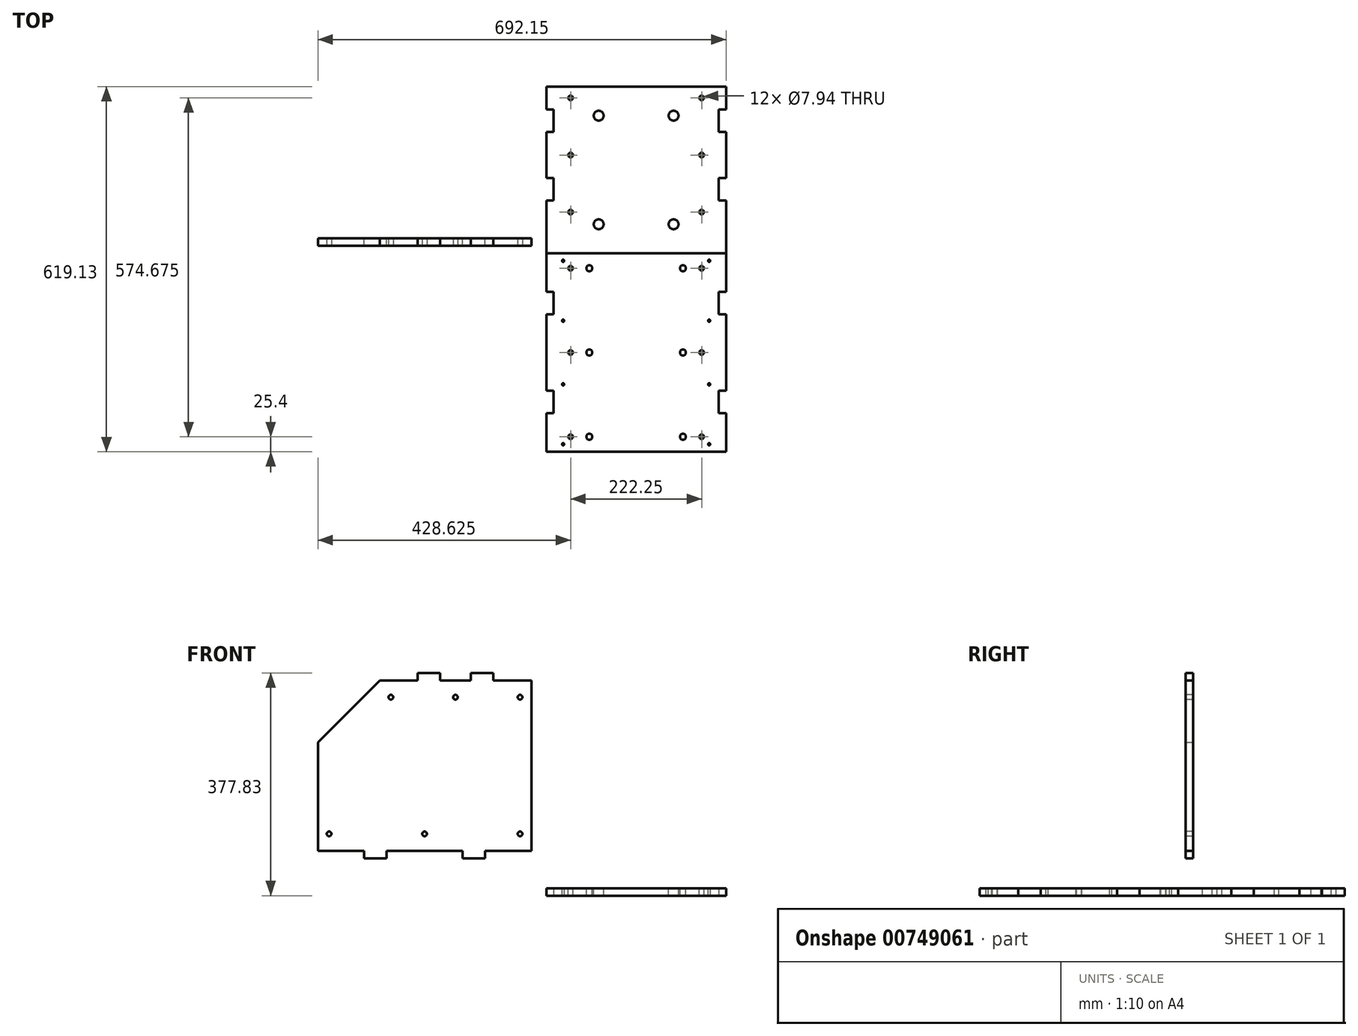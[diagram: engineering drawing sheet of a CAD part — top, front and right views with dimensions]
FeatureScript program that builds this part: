
annotation { "Feature Type Name" : "Feature", "Feature Type Description" : "" }
export const myFeature = defineFeature(function(context is Context, id is Id, definition is map)
    precondition{}
    {
        {
            var Q0;
            Q0=qCreatedBy(makeId("Front.planeOp"),FACE);
            var sketch = newSketch(context, id + "F0", { "sketchPlane" : qUnion([Q0])});
            skLineSegment(sketch, "E0", {"start": v(0, 76.2) * mm, "end": v(-78.1, 76.2) * mm});
            skLineSegment(sketch, "E1", {"start": v(-361.95, 76.2) * mm, "end": v(-361.95, 260.35) * mm});
            skLineSegment(sketch, "E2", {"start": v(-361.95, 260.35) * mm, "end": v(-257.18, 365.12) * mm});
            skLineSegment(sketch, "E3", {"start": v(-257.18, 365.12) * mm, "end": v(-192.85, 365.12) * mm});
            skLineSegment(sketch, "E4", {"start": v(0, 365.13) * mm, "end": v(0, 76.2) * mm});
            skLineSegment(sketch, "E5", {"start": v(-128.59, 365.13) * mm, "end": v(-128.59, 193.45) * mm, "construction": true});
            skLineSegment(sketch, "E6", {"start": v(-180.98, 76.2) * mm, "end": v(-180.98, 177) * mm, "construction": true});
            skLineSegment(sketch, "E7.top", {"start": v(-154.75, 377.83) * mm, "end": v(-192.85, 377.83) * mm});
            skLineSegment(sketch, "E7.left", {"start": v(-154.75, 365.13) * mm, "end": v(-154.75, 377.83) * mm});
            skLineSegment(sketch, "E7.right", {"start": v(-192.85, 365.12) * mm, "end": v(-192.85, 377.83) * mm});
            skPoint(sketch, "E7.middle", {"position": v(-199.2, 365.12) * mm});
            skLineSegment(sketch, "E8.MirrorCS", {"start": v(-102.43, 365.13) * mm, "end": v(-102.43, 377.82) * mm});
            skLineSegment(sketch, "E9.MirrorCS", {"start": v(-102.43, 377.83) * mm, "end": v(-64.33, 377.83) * mm});
            skLineSegment(sketch, "E10.MirrorCS", {"start": v(-64.33, 365.13) * mm, "end": v(-64.33, 377.83) * mm});
            skLineSegment(sketch, "E11.trimOffspring", {"start": v(-64.33, 365.13) * mm, "end": v(0, 365.13) * mm});
            skLineSegment(sketch, "E12.trimOffspring", {"start": v(-154.75, 365.13) * mm, "end": v(-102.43, 365.13) * mm});
            skLineSegment(sketch, "E13.bottom", {"start": v(-245.75, 63.5) * mm, "end": v(-283.85, 63.5) * mm});
            skLineSegment(sketch, "E13.left", {"start": v(-245.75, 63.5) * mm, "end": v(-245.75, 76.2) * mm});
            skLineSegment(sketch, "E13.right", {"start": v(-283.85, 63.5) * mm, "end": v(-283.85, 76.2) * mm});
            skPoint(sketch, "E13.middle", {"position": v(-264.8, 76.2) * mm});
            skLineSegment(sketch, "E14.trimOffspring", {"start": v(-283.85, 76.2) * mm, "end": v(-361.95, 76.2) * mm});
            skLineSegment(sketch, "E15.MirrorCS", {"start": v(-116.2, 63.5) * mm, "end": v(-116.2, 76.2) * mm});
            skLineSegment(sketch, "E16.MirrorCS", {"start": v(-116.2, 63.5) * mm, "end": v(-78.1, 63.5) * mm});
            skLineSegment(sketch, "E17.MirrorCS", {"start": v(-78.1, 63.5) * mm, "end": v(-78.1, 76.2) * mm});
            skLineSegment(sketch, "E18.trimOffspring", {"start": v(-116.2, 76.2) * mm, "end": v(-245.75, 76.2) * mm});
            skLineSegment(sketch, "E19", {"start": v(-361.95, 104.77) * mm, "end": v(0, 104.78) * mm, "construction": true});
            skLineSegment(sketch, "E20", {"start": v(0, 336.55) * mm, "end": v(-285.75, 336.55) * mm, "construction": true});
            skPoint(sketch, "E21", {"position": v(-128.59, 336.55) * mm});
            skPoint(sketch, "E22", {"position": v(-19.05, 336.55) * mm});
            skPoint(sketch, "E23", {"position": v(-19.05, 104.78) * mm});
            skPoint(sketch, "E24", {"position": v(-180.98, 104.77) * mm});
            skPoint(sketch, "E25.MirrorP", {"position": v(-238.13, 336.55) * mm});
            skPoint(sketch, "E26.MirrorP", {"position": v(-342.9, 104.78) * mm});
            skSolve(sketch);
        }
        {
            var Q0;
            Q0 = qSketchRegion(id + "F0", true);
            extrude(context, id + "F1", {"entities" : qUnion([Q0]), "depth" : 12.7 * mm, "offsetDistance" : 25.4 * mm});
        }
        {
            var Q0;
            Q0=qCreatedBy(makeId("Top.planeOp"),FACE);
            var sketch = newSketch(context, id + "F2", { "sketchPlane" : qUnion([Q0])});
            skLineSegment(sketch, "E27.bottom", {"start": v(25.4, 25.4) * mm, "end": v(330.2, 25.4) * mm});
            skLineSegment(sketch, "E27.top", {"start": v(25.4, 257.18) * mm, "end": v(330.2, 257.18) * mm});
            skLineSegment(sketch, "E27.left", {"start": v(25.4, 25.4) * mm, "end": v(25.4, 64.33) * mm});
            skLineSegment(sketch, "E27.right", {"start": v(330.2, 25.4) * mm, "end": v(330.2, 64.33) * mm});
            skLineSegment(sketch, "E28", {"start": v(177.8, 25.4) * mm, "end": v(177.8, 257.17) * mm, "construction": true});
            skLineSegment(sketch, "E29", {"start": v(25.4, 141.29) * mm, "end": v(330.2, 141.29) * mm, "construction": true});
            skLineSegment(sketch, "E30.bottom", {"start": v(38.1, 180.15) * mm, "end": v(25.4, 180.15) * mm});
            skLineSegment(sketch, "E30.top", {"start": v(38.1, 218.25) * mm, "end": v(25.4, 218.25) * mm});
            skLineSegment(sketch, "E30.left", {"start": v(38.1, 180.15) * mm, "end": v(38.1, 218.25) * mm});
            skPoint(sketch, "E30.middle", {"position": v(25.4, 199.2) * mm});
            skPoint(sketch, "E31.orphan", {"position": v(12.7, 218.25) * mm});
            skLineSegment(sketch, "E32.trimOffspring", {"start": v(25.4, 218.25) * mm, "end": v(25.4, 257.18) * mm});
            skPoint(sketch, "E33.orphan", {"position": v(12.7, 180.15) * mm});
            skLineSegment(sketch, "E34.MirrorCS", {"start": v(317.5, 180.15) * mm, "end": v(317.5, 218.25) * mm});
            skLineSegment(sketch, "E35.MirrorCS", {"start": v(317.5, 218.25) * mm, "end": v(330.2, 218.25) * mm});
            skLineSegment(sketch, "E36.MirrorCS", {"start": v(317.5, 180.15) * mm, "end": v(330.2, 180.15) * mm});
            skLineSegment(sketch, "E37.MirrorCS", {"start": v(38.1, 102.43) * mm, "end": v(25.4, 102.43) * mm});
            skLineSegment(sketch, "E38.MirrorCS", {"start": v(38.1, 102.43) * mm, "end": v(38.1, 64.33) * mm});
            skLineSegment(sketch, "E39.MirrorCS", {"start": v(38.1, 64.33) * mm, "end": v(25.4, 64.33) * mm});
            skLineSegment(sketch, "E40.MirrorCS", {"start": v(317.5, 102.43) * mm, "end": v(317.5, 64.33) * mm});
            skLineSegment(sketch, "E41.MirrorCS", {"start": v(317.5, 64.33) * mm, "end": v(330.2, 64.33) * mm});
            skLineSegment(sketch, "E42.MirrorCS", {"start": v(317.5, 102.43) * mm, "end": v(330.2, 102.43) * mm});
            skLineSegment(sketch, "E43.trimOffspring", {"start": v(25.4, 102.43) * mm, "end": v(25.4, 199.2) * mm});
            skLineSegment(sketch, "E44.trimOffspring", {"start": v(330.2, 102.43) * mm, "end": v(330.2, 180.15) * mm});
            skLineSegment(sketch, "E45.trimOffspring", {"start": v(330.2, 218.25) * mm, "end": v(330.2, 257.18) * mm});
            skPoint(sketch, "E46", {"position": v(241.3, 207.96) * mm});
            skPoint(sketch, "E47", {"position": v(241.3, 23.81) * mm});
            skPoint(sketch, "E48.MirrorP", {"position": v(114.3, 207.96) * mm});
            skPoint(sketch, "E49.MirrorP", {"position": v(114.3, 23.81) * mm});
            skPoint(sketch, "E50", {"position": v(66.67, 238.13) * mm});
            skPoint(sketch, "E51", {"position": v(66.67, 141.29) * mm});
            skPoint(sketch, "E52.MirrorP", {"position": v(66.68, 44.45) * mm});
            skPoint(sketch, "E53.MirrorP", {"position": v(288.92, 238.13) * mm});
            skPoint(sketch, "E54.MirrorP", {"position": v(288.93, 141.29) * mm});
            skPoint(sketch, "E55.MirrorP", {"position": v(288.93, 44.45) * mm});
            skLineSegment(sketch, "E56.top", {"start": v(25.4, -25.4) * mm, "end": v(330.2, -25.4) * mm});
            skLineSegment(sketch, "E56.left", {"start": v(25.4, 25.4) * mm, "end": v(25.4, -25.4) * mm});
            skLineSegment(sketch, "E56.right", {"start": v(330.2, 25.4) * mm, "end": v(330.2, -25.4) * mm});
            skSolve(sketch);
        }
        {
            var Q0;
            Q0 = qSketchRegion(id + "F2", true);
            extrude(context, id + "F3", {"entities" : qUnion([Q0]), "depth" : 12.7 * mm, "offsetDistance" : 25.4 * mm});
        }
        {
            var Q0;
            Q0=sQuery(id+"F2.wireOp",VERTEX,"E50");
            var Q1;
            Q1=sQuery(id+"F2.wireOp",VERTEX,"E51");
            var Q2;
            Q2=sQuery(id+"F2.wireOp",VERTEX,"E52.MirrorP");
            var Q3;
            Q3=sQuery(id+"F2.wireOp",VERTEX,"E53.MirrorP");
            var Q4;
            Q4=sQuery(id+"F2.wireOp",VERTEX,"E54.MirrorP");
            var Q5;
            Q5=sQuery(id+"F2.wireOp",VERTEX,"E55.MirrorP");
            var Q6;
            Q6=makeQuery(id+"F3.opExtrude","SWEPT_BODY",BODY,{"disambiguationData":[OSD([sQuery(id+"F2.wireOp",EDGE,"E27.bottom"),sQuery(id+"F2.wireOp",EDGE,"E27.top"),sQuery(id+"F2.wireOp",EDGE,"E27.left"),sQuery(id+"F2.wireOp",EDGE,"E27.right"),sQuery(id+"F2.wireOp",EDGE,"E30.bottom"),sQuery(id+"F2.wireOp",EDGE,"E30.top"),sQuery(id+"F2.wireOp",EDGE,"E30.left"),sQuery(id+"F2.wireOp",EDGE,"E32.trimOffspring"),sQuery(id+"F2.wireOp",EDGE,"E34.MirrorCS"),sQuery(id+"F2.wireOp",EDGE,"E35.MirrorCS"),sQuery(id+"F2.wireOp",EDGE,"E36.MirrorCS"),sQuery(id+"F2.wireOp",EDGE,"E37.MirrorCS"),sQuery(id+"F2.wireOp",EDGE,"E38.MirrorCS"),sQuery(id+"F2.wireOp",EDGE,"E39.MirrorCS"),sQuery(id+"F2.wireOp",EDGE,"E41.MirrorCS"),sQuery(id+"F2.wireOp",EDGE,"E40.MirrorCS"),sQuery(id+"F2.wireOp",EDGE,"E42.MirrorCS"),sQuery(id+"F2.wireOp",EDGE,"E43.trimOffspring"),sQuery(id+"F2.wireOp",EDGE,"E44.trimOffspring"),sQuery(id+"F2.wireOp",EDGE,"E45.trimOffspring")])]});
            hole(context, id + "F4", {"style" : HoleStyle.SIMPLE, "endStyle" : HoleEndStyle.BLIND, "oppositeDirection" : true, "standardTappedOrClearance" : lookupTablePath({ "standard" : "ANSI", "engagement" : "75%", "pitch" : "16 tpi", "size" : "3/8", "type" : "Tapped" }), "standardBlindInLast" : lookupTablePath({ "standard" : "ANSI", "engagement" : "75%", "pitch" : "16 tpi", "size" : "3/8", "type" : "Tapped" }), "holeDiameter" : 7.94 * mm, "majorDiameter" : 9.52 * mm, "showTappedDepth" : true, "holeDepth" : 20.65 * mm, "isTappedThrough" : true, "tappedDepth" : 15.9 * mm, "tapClearance" : 3, "locations" : qUnion([Q0, Q1, Q2, Q3, Q4, Q5]), "scope" : qUnion([Q6])});
        }
        {
            var Q0;
            Q0=sQuery(id+"F2.wireOp",VERTEX,"E48.MirrorP");
            var Q1;
            Q1=sQuery(id+"F2.wireOp",VERTEX,"E49.MirrorP");
            var Q2;
            Q2=sQuery(id+"F2.wireOp",VERTEX,"E47");
            var Q3;
            Q3=sQuery(id+"F2.wireOp",VERTEX,"E46");
            var Q4;
            Q4=makeQuery(id+"F3.opExtrude","SWEPT_BODY",BODY,{"disambiguationData":[OSD([sQuery(id+"F2.wireOp",EDGE,"E27.bottom"),sQuery(id+"F2.wireOp",EDGE,"E27.top"),sQuery(id+"F2.wireOp",EDGE,"E27.left"),sQuery(id+"F2.wireOp",EDGE,"E27.right"),sQuery(id+"F2.wireOp",EDGE,"E30.bottom"),sQuery(id+"F2.wireOp",EDGE,"E30.top"),sQuery(id+"F2.wireOp",EDGE,"E30.left"),sQuery(id+"F2.wireOp",EDGE,"E32.trimOffspring"),sQuery(id+"F2.wireOp",EDGE,"E34.MirrorCS"),sQuery(id+"F2.wireOp",EDGE,"E35.MirrorCS"),sQuery(id+"F2.wireOp",EDGE,"E36.MirrorCS"),sQuery(id+"F2.wireOp",EDGE,"E37.MirrorCS"),sQuery(id+"F2.wireOp",EDGE,"E38.MirrorCS"),sQuery(id+"F2.wireOp",EDGE,"E39.MirrorCS"),sQuery(id+"F2.wireOp",EDGE,"E41.MirrorCS"),sQuery(id+"F2.wireOp",EDGE,"E40.MirrorCS"),sQuery(id+"F2.wireOp",EDGE,"E42.MirrorCS"),sQuery(id+"F2.wireOp",EDGE,"E43.trimOffspring"),sQuery(id+"F2.wireOp",EDGE,"E44.trimOffspring"),sQuery(id+"F2.wireOp",EDGE,"E45.trimOffspring")])]});
            hole(context, id + "F5", {"style" : HoleStyle.SIMPLE, "endStyle" : HoleEndStyle.BLIND, "oppositeDirection" : true, "standardTappedOrClearance" : lookupTablePath({ "fit" : "Normal (ASME)", "standard" : "ANSI", "size" : "5/8", "type" : "Clearance" }), "standardBlindInLast" : lookupTablePath({ "fit" : "Free", "standard" : "ANSI", "size" : "5/8", "type" : "Clearance" }), "holeDiameter" : 16.67 * mm, "majorDiameter" : 15.88 * mm, "holeDepth" : 22.8 * mm, "isTappedThrough" : true, "tappedDepth" : 15.9 * mm, "tapClearance" : 3, "locations" : qUnion([Q0, Q1, Q2, Q3]), "scope" : qUnion([Q4])});
        }
        {
            var Q0;
            Q0=qCreatedBy(makeId("Top.planeOp"),FACE);
            var sketch = newSketch(context, id + "F6", { "sketchPlane" : qUnion([Q0])});
            skLineSegment(sketch, "E57.bottom", {"start": v(25.4, -25.4) * mm, "end": v(330.2, -25.4) * mm});
            skLineSegment(sketch, "E57.top", {"start": v(25.4, -361.95) * mm, "end": v(330.2, -361.95) * mm});
            skLineSegment(sketch, "E57.left", {"start": v(25.4, -25.4) * mm, "end": v(25.4, -90.8) * mm});
            skLineSegment(sketch, "E57.right", {"start": v(330.2, -25.4) * mm, "end": v(330.2, -90.8) * mm});
            skLineSegment(sketch, "E58", {"start": v(177.8, -361.95) * mm, "end": v(177.8, -25.4) * mm, "construction": true});
            skLineSegment(sketch, "E59", {"start": v(330.2, -193.67) * mm, "end": v(25.4, -193.67) * mm, "construction": true});
            skLineSegment(sketch, "E60.bottom", {"start": v(317.5, -258.44) * mm, "end": v(330.2, -258.44) * mm});
            skLineSegment(sketch, "E60.top", {"start": v(317.5, -296.54) * mm, "end": v(330.2, -296.54) * mm});
            skLineSegment(sketch, "E60.left", {"start": v(317.5, -258.44) * mm, "end": v(317.5, -296.54) * mm});
            skPoint(sketch, "E60.middle", {"position": v(330.2, -277.5) * mm});
            skPoint(sketch, "E61.orphan", {"position": v(342.9, -296.54) * mm});
            skPoint(sketch, "E62.orphan", {"position": v(342.9, -258.44) * mm});
            skLineSegment(sketch, "E63.trimOffspring", {"start": v(330.2, -296.54) * mm, "end": v(330.2, -361.95) * mm});
            skLineSegment(sketch, "E64.MirrorCS", {"start": v(38.1, -296.54) * mm, "end": v(25.4, -296.54) * mm});
            skLineSegment(sketch, "E65.MirrorCS", {"start": v(38.1, -258.44) * mm, "end": v(38.1, -296.54) * mm});
            skLineSegment(sketch, "E66.MirrorCS", {"start": v(38.1, -258.44) * mm, "end": v(25.4, -258.44) * mm});
            skLineSegment(sketch, "E67.trimOffspring", {"start": v(25.4, -296.54) * mm, "end": v(25.4, -361.95) * mm});
            skLineSegment(sketch, "E68.MirrorCS", {"start": v(317.5, -128.9) * mm, "end": v(330.2, -128.9) * mm});
            skLineSegment(sketch, "E69.MirrorCS", {"start": v(317.5, -128.9) * mm, "end": v(317.5, -90.8) * mm});
            skLineSegment(sketch, "E70.MirrorCS", {"start": v(317.5, -90.8) * mm, "end": v(330.2, -90.8) * mm});
            skLineSegment(sketch, "E71.MirrorCS", {"start": v(38.1, -128.9) * mm, "end": v(38.1, -90.8) * mm});
            skLineSegment(sketch, "E72.MirrorCS", {"start": v(38.1, -90.8) * mm, "end": v(25.4, -90.8) * mm});
            skLineSegment(sketch, "E73.MirrorCS", {"start": v(38.1, -128.9) * mm, "end": v(25.4, -128.9) * mm});
            skLineSegment(sketch, "E74.trimOffspring", {"start": v(330.2, -128.9) * mm, "end": v(330.2, -258.44) * mm});
            skLineSegment(sketch, "E75.trimOffspring", {"start": v(25.4, -128.9) * mm, "end": v(25.4, -258.44) * mm});
            skPoint(sketch, "E76", {"position": v(66.68, -336.55) * mm});
            skPoint(sketch, "E77", {"position": v(66.68, -193.67) * mm});
            skPoint(sketch, "E78.MirrorP", {"position": v(66.67, -50.8) * mm});
            skPoint(sketch, "E79.MirrorP", {"position": v(288.93, -336.55) * mm});
            skPoint(sketch, "E80.MirrorP", {"position": v(288.93, -193.67) * mm});
            skPoint(sketch, "E81.MirrorP", {"position": v(288.93, -50.8) * mm});
            skPoint(sketch, "E82", {"position": v(98.43, -336.55) * mm});
            skPoint(sketch, "E83", {"position": v(98.42, -193.67) * mm});
            skPoint(sketch, "E84.MirrorP", {"position": v(98.42, -50.8) * mm});
            skPoint(sketch, "E85", {"position": v(53.98, -349.25) * mm});
            skPoint(sketch, "E86.MirrorP", {"position": v(53.97, -38.1) * mm});
            skPoint(sketch, "E87", {"position": v(53.98, -247.65) * mm});
            skPoint(sketch, "E88.MirrorP", {"position": v(53.97, -139.7) * mm});
            skLineSegment(sketch, "E89.MirrorCS", {"start": v(177.8, -25.4) * mm, "end": v(177.8, -361.95) * mm, "construction": true});
            skPoint(sketch, "E90.MirrorP", {"position": v(257.18, -193.67) * mm});
            skPoint(sketch, "E91.MirrorP", {"position": v(301.62, -139.7) * mm});
            skPoint(sketch, "E92.MirrorP", {"position": v(288.92, -50.8) * mm});
            skPoint(sketch, "E93.MirrorP", {"position": v(301.62, -38.1) * mm});
            skPoint(sketch, "E94.MirrorP", {"position": v(301.63, -247.65) * mm});
            skPoint(sketch, "E95.MirrorP", {"position": v(301.63, -349.25) * mm});
            skPoint(sketch, "E96.MirrorP", {"position": v(257.18, -336.55) * mm});
            skPoint(sketch, "E97.MirrorP", {"position": v(257.17, -50.8) * mm});
            skSolve(sketch);
        }
        {
            var Q0;
            Q0=sQuery(id+"F0.wireOp",VERTEX,"E25.MirrorP");
            var Q1;
            Q1=sQuery(id+"F0.wireOp",VERTEX,"E22");
            var Q2;
            Q2=sQuery(id+"F0.wireOp",VERTEX,"E21");
            var Q3;
            Q3=sQuery(id+"F0.wireOp",VERTEX,"E26.MirrorP");
            var Q4;
            Q4=sQuery(id+"F0.wireOp",VERTEX,"E24");
            var Q5;
            Q5=sQuery(id+"F0.wireOp",VERTEX,"E23");
            var Q6;
            Q6=makeQuery(id+"F1.opExtrude","SWEPT_BODY",BODY,{"disambiguationData":[OSD([sQuery(id+"F0.wireOp",EDGE,"E0"),sQuery(id+"F0.wireOp",EDGE,"E1"),sQuery(id+"F0.wireOp",EDGE,"E2"),sQuery(id+"F0.wireOp",EDGE,"E3"),sQuery(id+"F0.wireOp",EDGE,"E4"),sQuery(id+"F0.wireOp",EDGE,"E7.top"),sQuery(id+"F0.wireOp",EDGE,"E7.left"),sQuery(id+"F0.wireOp",EDGE,"E7.right"),sQuery(id+"F0.wireOp",EDGE,"E8.MirrorCS"),sQuery(id+"F0.wireOp",EDGE,"E9.MirrorCS"),sQuery(id+"F0.wireOp",EDGE,"E10.MirrorCS"),sQuery(id+"F0.wireOp",EDGE,"E11.trimOffspring"),sQuery(id+"F0.wireOp",EDGE,"E12.trimOffspring"),sQuery(id+"F0.wireOp",EDGE,"E13.bottom"),sQuery(id+"F0.wireOp",EDGE,"E13.left"),sQuery(id+"F0.wireOp",EDGE,"E13.right"),sQuery(id+"F0.wireOp",EDGE,"E14.trimOffspring"),sQuery(id+"F0.wireOp",EDGE,"E15.MirrorCS"),sQuery(id+"F0.wireOp",EDGE,"E16.MirrorCS"),sQuery(id+"F0.wireOp",EDGE,"E17.MirrorCS"),sQuery(id+"F0.wireOp",EDGE,"E18.trimOffspring")])]});
            hole(context, id + "F7", {"style" : HoleStyle.SIMPLE, "endStyle" : HoleEndStyle.BLIND, "oppositeDirection" : true, "standardTappedOrClearance" : lookupTablePath({ "standard" : "ANSI", "engagement" : "75%", "pitch" : "16 tpi", "size" : "3/8", "type" : "Tapped" }), "standardBlindInLast" : lookupTablePath({ "standard" : "ANSI", "engagement" : "75%", "pitch" : "16 tpi", "size" : "3/8", "type" : "Tapped" }), "holeDiameter" : 7.94 * mm, "majorDiameter" : 9.52 * mm, "showTappedDepth" : true, "holeDepth" : 20.66 * mm, "isTappedThrough" : true, "tappedDepth" : 15.9 * mm, "tapClearance" : 3, "locations" : qUnion([Q0, Q1, Q2, Q3, Q4, Q5]), "scope" : qUnion([Q6])});
        }
        {
            var Q0;
            Q0 = qSketchRegion(id + "F6", true);
            extrude(context, id + "F8", {"entities" : qUnion([Q0]), "depth" : 12.7 * mm, "offsetDistance" : 25.4 * mm});
        }
        {
            var Q0;
            Q0=sQuery(id+"F6.wireOp",VERTEX,"E95.MirrorP");
            var Q1;
            Q1=sQuery(id+"F6.wireOp",VERTEX,"E94.MirrorP");
            var Q2;
            Q2=sQuery(id+"F6.wireOp",VERTEX,"E91.MirrorP");
            var Q3;
            Q3=sQuery(id+"F6.wireOp",VERTEX,"E93.MirrorP");
            var Q4;
            Q4=sQuery(id+"F6.wireOp",VERTEX,"E85");
            var Q5;
            Q5=sQuery(id+"F6.wireOp",VERTEX,"E87");
            var Q6;
            Q6=sQuery(id+"F6.wireOp",VERTEX,"E88.MirrorP");
            var Q7;
            Q7=sQuery(id+"F6.wireOp",VERTEX,"E86.MirrorP");
            var Q8;
            Q8=makeQuery(id+"F8.opExtrude","SWEPT_BODY",BODY,{"disambiguationData":[OSD([sQuery(id+"F6.wireOp",EDGE,"E57.bottom"),sQuery(id+"F6.wireOp",EDGE,"E57.top"),sQuery(id+"F6.wireOp",EDGE,"E57.left"),sQuery(id+"F6.wireOp",EDGE,"E57.right"),sQuery(id+"F6.wireOp",EDGE,"E60.bottom"),sQuery(id+"F6.wireOp",EDGE,"E60.top"),sQuery(id+"F6.wireOp",EDGE,"E60.left"),sQuery(id+"F6.wireOp",EDGE,"E63.trimOffspring"),sQuery(id+"F6.wireOp",EDGE,"E64.MirrorCS"),sQuery(id+"F6.wireOp",EDGE,"E65.MirrorCS"),sQuery(id+"F6.wireOp",EDGE,"E66.MirrorCS"),sQuery(id+"F6.wireOp",EDGE,"E67.trimOffspring"),sQuery(id+"F6.wireOp",EDGE,"E68.MirrorCS"),sQuery(id+"F6.wireOp",EDGE,"E69.MirrorCS"),sQuery(id+"F6.wireOp",EDGE,"E70.MirrorCS"),sQuery(id+"F6.wireOp",EDGE,"E71.MirrorCS"),sQuery(id+"F6.wireOp",EDGE,"E72.MirrorCS"),sQuery(id+"F6.wireOp",EDGE,"E73.MirrorCS"),sQuery(id+"F6.wireOp",EDGE,"E74.trimOffspring"),sQuery(id+"F6.wireOp",EDGE,"E75.trimOffspring")])]});
            hole(context, id + "F9", {"style" : HoleStyle.SIMPLE, "endStyle" : HoleEndStyle.BLIND, "oppositeDirection" : true, "standardTappedOrClearance" : lookupTablePath({ "standard" : "ANSI", "engagement" : "75%", "pitch" : "24 tpi", "size" : "#10", "type" : "Tapped" }), "standardBlindInLast" : lookupTablePath({ "standard" : "ANSI", "engagement" : "75%", "pitch" : "24 tpi", "size" : "#10", "type" : "Tapped" }), "holeDiameter" : 3.8 * mm, "majorDiameter" : 4.83 * mm, "showTappedDepth" : true, "holeDepth" : 19.09 * mm, "isTappedThrough" : true, "tappedDepth" : 15.9 * mm, "tapClearance" : 3, "locations" : qUnion([Q0, Q1, Q2, Q3, Q4, Q5, Q6, Q7]), "scope" : qUnion([Q8])});
        }
        {
            var Q0;
            Q0=sQuery(id+"F6.wireOp",VERTEX,"E79.MirrorP");
            var Q1;
            Q1=sQuery(id+"F6.wireOp",VERTEX,"E80.MirrorP");
            var Q2;
            Q2=sQuery(id+"F6.wireOp",VERTEX,"E81.MirrorP");
            var Q3;
            Q3=sQuery(id+"F6.wireOp",VERTEX,"E76");
            var Q4;
            Q4=sQuery(id+"F6.wireOp",VERTEX,"E77");
            var Q5;
            Q5=sQuery(id+"F6.wireOp",VERTEX,"E78.MirrorP");
            var Q6;
            Q6=makeQuery(id+"F8.opExtrude","SWEPT_BODY",BODY,{"disambiguationData":[OSD([sQuery(id+"F6.wireOp",EDGE,"E57.bottom"),sQuery(id+"F6.wireOp",EDGE,"E57.top"),sQuery(id+"F6.wireOp",EDGE,"E57.left"),sQuery(id+"F6.wireOp",EDGE,"E57.right"),sQuery(id+"F6.wireOp",EDGE,"E60.bottom"),sQuery(id+"F6.wireOp",EDGE,"E60.top"),sQuery(id+"F6.wireOp",EDGE,"E60.left"),sQuery(id+"F6.wireOp",EDGE,"E63.trimOffspring"),sQuery(id+"F6.wireOp",EDGE,"E64.MirrorCS"),sQuery(id+"F6.wireOp",EDGE,"E65.MirrorCS"),sQuery(id+"F6.wireOp",EDGE,"E66.MirrorCS"),sQuery(id+"F6.wireOp",EDGE,"E67.trimOffspring"),sQuery(id+"F6.wireOp",EDGE,"E68.MirrorCS"),sQuery(id+"F6.wireOp",EDGE,"E69.MirrorCS"),sQuery(id+"F6.wireOp",EDGE,"E70.MirrorCS"),sQuery(id+"F6.wireOp",EDGE,"E71.MirrorCS"),sQuery(id+"F6.wireOp",EDGE,"E72.MirrorCS"),sQuery(id+"F6.wireOp",EDGE,"E73.MirrorCS"),sQuery(id+"F6.wireOp",EDGE,"E74.trimOffspring"),sQuery(id+"F6.wireOp",EDGE,"E75.trimOffspring")])]});
            hole(context, id + "F10", {"style" : HoleStyle.SIMPLE, "endStyle" : HoleEndStyle.BLIND, "oppositeDirection" : true, "standardTappedOrClearance" : lookupTablePath({ "standard" : "ANSI", "engagement" : "75%", "pitch" : "16 tpi", "size" : "3/8", "type" : "Tapped" }), "standardBlindInLast" : lookupTablePath({ "standard" : "ANSI", "engagement" : "75%", "pitch" : "16 tpi", "size" : "3/8", "type" : "Tapped" }), "holeDiameter" : 7.94 * mm, "majorDiameter" : 9.52 * mm, "showTappedDepth" : true, "holeDepth" : 22.26 * mm, "isTappedThrough" : true, "tappedDepth" : 17.5 * mm, "tapClearance" : 3, "locations" : qUnion([Q0, Q1, Q2, Q3, Q4, Q5]), "scope" : qUnion([Q6])});
        }
        {
            var Q0;
            Q0=sQuery(id+"F6.wireOp",VERTEX,"E96.MirrorP");
            var Q1;
            Q1=sQuery(id+"F6.wireOp",VERTEX,"E90.MirrorP");
            var Q2;
            Q2=sQuery(id+"F6.wireOp",VERTEX,"E83");
            var Q3;
            Q3=sQuery(id+"F6.wireOp",VERTEX,"E82");
            var Q4;
            Q4=sQuery(id+"F6.wireOp",VERTEX,"E84.MirrorP");
            var Q5;
            Q5=sQuery(id+"F6.wireOp",VERTEX,"E97.MirrorP");
            var Q6;
            Q6=makeQuery(id+"F8.opExtrude","SWEPT_BODY",BODY,{"disambiguationData":[OSD([sQuery(id+"F6.wireOp",EDGE,"E57.bottom"),sQuery(id+"F6.wireOp",EDGE,"E57.top"),sQuery(id+"F6.wireOp",EDGE,"E57.left"),sQuery(id+"F6.wireOp",EDGE,"E57.right"),sQuery(id+"F6.wireOp",EDGE,"E60.bottom"),sQuery(id+"F6.wireOp",EDGE,"E60.top"),sQuery(id+"F6.wireOp",EDGE,"E60.left"),sQuery(id+"F6.wireOp",EDGE,"E63.trimOffspring"),sQuery(id+"F6.wireOp",EDGE,"E64.MirrorCS"),sQuery(id+"F6.wireOp",EDGE,"E65.MirrorCS"),sQuery(id+"F6.wireOp",EDGE,"E66.MirrorCS"),sQuery(id+"F6.wireOp",EDGE,"E67.trimOffspring"),sQuery(id+"F6.wireOp",EDGE,"E68.MirrorCS"),sQuery(id+"F6.wireOp",EDGE,"E69.MirrorCS"),sQuery(id+"F6.wireOp",EDGE,"E70.MirrorCS"),sQuery(id+"F6.wireOp",EDGE,"E71.MirrorCS"),sQuery(id+"F6.wireOp",EDGE,"E72.MirrorCS"),sQuery(id+"F6.wireOp",EDGE,"E73.MirrorCS"),sQuery(id+"F6.wireOp",EDGE,"E74.trimOffspring"),sQuery(id+"F6.wireOp",EDGE,"E75.trimOffspring")])]});
            hole(context, id + "F11", {"style" : HoleStyle.SIMPLE, "endStyle" : HoleEndStyle.BLIND, "oppositeDirection" : true, "standardTappedOrClearance" : lookupTablePath({ "fit" : "Normal (ASME)", "standard" : "ANSI", "size" : "3/8", "type" : "Clearance" }), "standardBlindInLast" : lookupTablePath({ "fit" : "Free", "standard" : "ANSI", "size" : "3/8", "type" : "Clearance" }), "holeDiameter" : 10.08 * mm, "majorDiameter" : 9.52 * mm, "holeDepth" : 22.28 * mm, "isTappedThrough" : true, "tappedDepth" : 17.51 * mm, "tapClearance" : 3, "locations" : qUnion([Q0, Q1, Q2, Q3, Q4, Q5]), "scope" : qUnion([Q6])});
        }
    });
